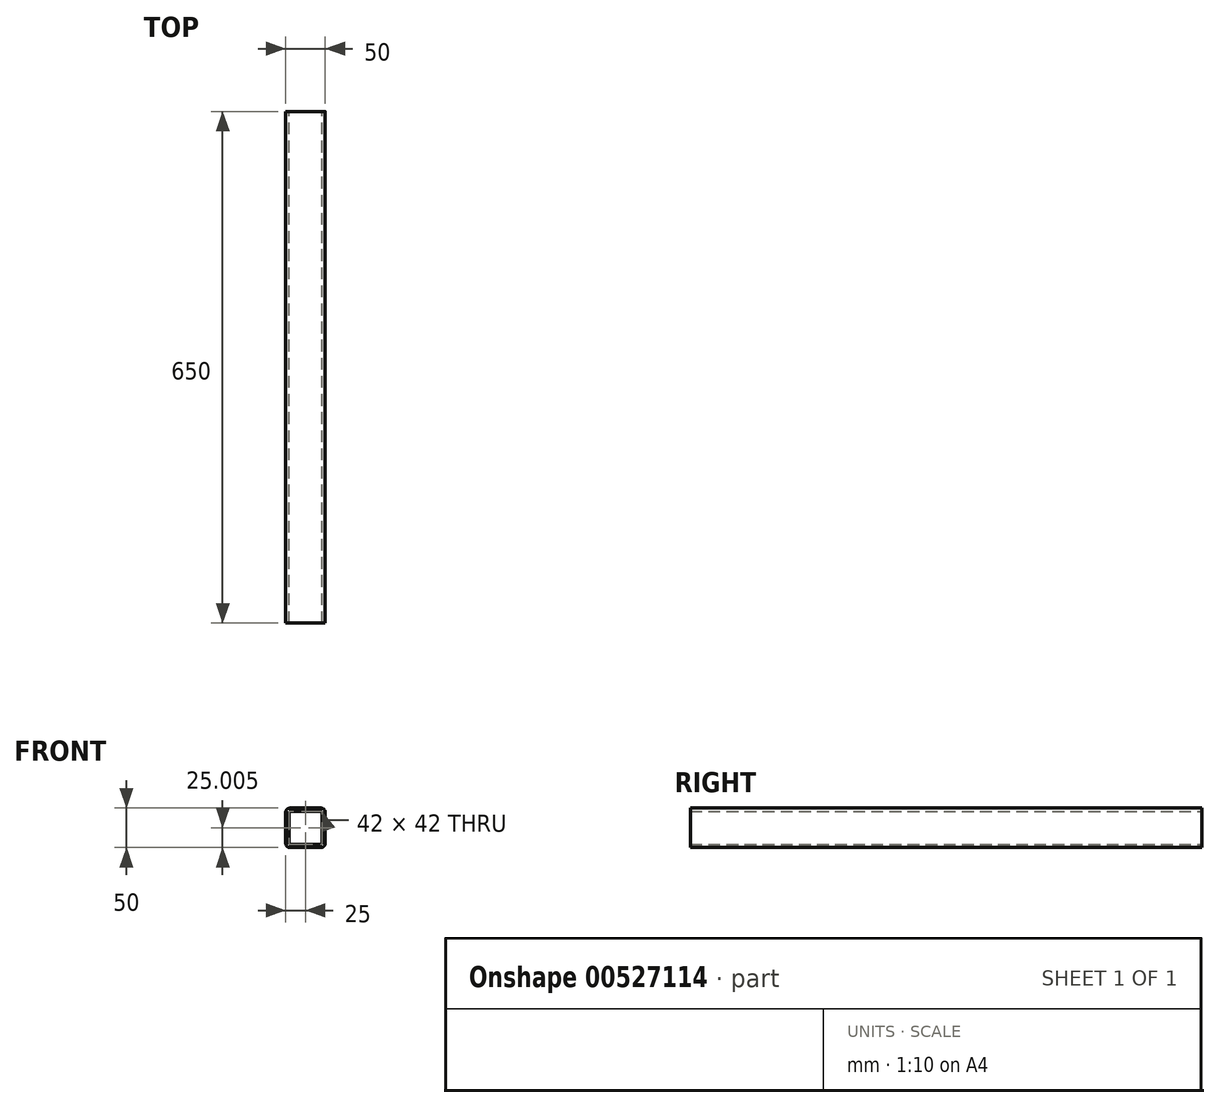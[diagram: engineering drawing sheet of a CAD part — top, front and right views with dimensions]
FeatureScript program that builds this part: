
annotation { "Feature Type Name" : "Feature", "Feature Type Description" : "" }
export const myFeature = defineFeature(function(context is Context, id is Id, definition is map)
    precondition{}
    {
        {
            var Q0;
            Q0=qCreatedBy(makeId("Front.planeOp"),FACE);
            var sketch = newSketch(context, id + "F0", { "sketchPlane" : qUnion([Q0])});
            skLineSegment(sketch, "E0.0", {"start": v(-20, 26.3) * mm, "end": v(0, 26.3) * mm});
            skLineSegment(sketch, "E1.0", {"start": v(-25, -18.7) * mm, "end": v(-25, 21.3) * mm});
            skLineSegment(sketch, "E2.0", {"start": v(-20, -23.7) * mm, "end": v(0, -23.7) * mm});
            skPoint(sketch, "E3.visualSharp", {"position": v(-25, -23.7) * mm});
            skArc(sketch, "E3.filletArc", {"start": v(-25, -18.7) * mm, "mid": v(-23.54, -22.23) * mm, "end": v(-20, -23.7) * mm});
            skPoint(sketch, "E4.visualSharp", {"position": v(-25, 26.3) * mm});
            skArc(sketch, "E4.filletArc", {"start": v(-20, 26.3) * mm, "mid": v(-23.54, 24.84) * mm, "end": v(-25, 21.3) * mm});
            skLineSegment(sketch, "E5", {"start": v(0, 26.3) * mm, "end": v(0, -26.3) * mm, "construction": true});
            skPoint(sketch, "E5.endSnap0", {"position": v(0, -23.7) * mm});
            skLineSegment(sketch, "E6.MirrorCS", {"start": v(20, 26.3) * mm, "end": v(0, 26.3) * mm});
            skArc(sketch, "E7.MirrorCS", {"start": v(20, 26.3) * mm, "mid": v(23.54, 24.84) * mm, "end": v(25, 21.3) * mm});
            skLineSegment(sketch, "E8.MirrorCS", {"start": v(25, -18.7) * mm, "end": v(25, 21.3) * mm});
            skArc(sketch, "E9.MirrorCS", {"start": v(25, -18.7) * mm, "mid": v(23.54, -22.23) * mm, "end": v(20, -23.7) * mm});
            skLineSegment(sketch, "E10.MirrorCS", {"start": v(20, -23.7) * mm, "end": v(0, -23.7) * mm});
            skLineSegment(sketch, "E11.0", {"start": v(-21, 22.3) * mm, "end": v(2.5, 22.3) * mm});
            skLineSegment(sketch, "E11.1", {"start": v(21, -19.7) * mm, "end": v(21, 22.3) * mm});
            skLineSegment(sketch, "E11.2", {"start": v(21, -19.7) * mm, "end": v(2.5, -19.7) * mm});
            skLineSegment(sketch, "E11.3", {"start": v(21, 22.3) * mm, "end": v(2.5, 22.3) * mm});
            skLineSegment(sketch, "E11.4", {"start": v(-21, -19.7) * mm, "end": v(2.5, -19.7) * mm});
            skLineSegment(sketch, "E11.5", {"start": v(-21, -19.7) * mm, "end": v(-21, 22.3) * mm});
            skSolve(sketch);
        }
        {
            var Q0;
            Q0=makeQuery(id+"F0.imprint","IMPRINT",FACE,{"disambiguationData":[TD([[makeQuery(id+"F0.imprint","IMPRINT",EDGE,{"derivedFrom":sQuery(id+"F0.wireOp",EDGE,"E0.0")}),-1.0]])]});
            extrude(context, id + "F1", {"entities" : qUnion([Q0]), "depth" : 650 * mm, "offsetDistance" : 25 * mm});
        }
    });
